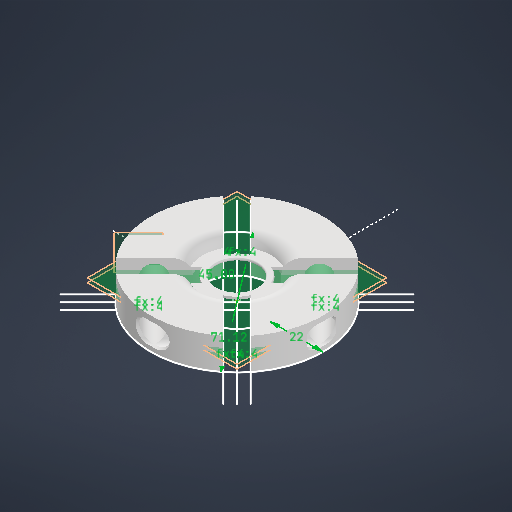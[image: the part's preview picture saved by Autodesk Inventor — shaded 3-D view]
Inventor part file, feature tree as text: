
AUTODESK INVENTOR PART (.ipt)
format: ipt  version: 2025 (Build 290162010, 162A)  size: 385,536 bytes
history: native  units: mm
features: extrude x4, sketch x3, plane x3, fillet x3, mirror x2
ambient origin geometry x8: Origin, YZ Plane, XZ Plane, XY Plane, X Axis, Y Axis, Z Axis, Center Point
bodies: Solid1 (feature_tree)
feature tree (15):
  sketch  "Sketch1"  dims[d0=71.12mm d1=22.0mm]
  extrude  "Extrusion1"  Depth=22.0mm
  extrude  "Extrusion2"  TaperAngle=45.0deg  [1 undecoded]
  plane  "Work Plane1"
  extrude  "Extrusion3"  Depth=0.5mm
  mirror  "Mirror1"
  mirror  "Mirror2"
  fillet  "Fillet1"  Radius=4.0mm
  plane  "Work Plane3"
  extrude  "Extrusion5"  Depth=0.5mm
  fillet  "Fillet3"  Radius=4.0mm
  fillet  "Fillet4"  Radius=4.0mm
  sketch  "Sketch2"  dims[d2=13.0mm d3=0.0mm d4=45.0deg]
  plane  "Work Plane2"
  sketch  "Sketch4"  dims[d5=4.0mm d6=4.0mm d7=4.0mm d8=4.0mm d9=4.0mm d10=4.0mm d11=4.0mm d12=4.0mm d13=13.0mm d14=0.0mm d15=20.0mm d16=9.0mm d17=13.0mm d18=50.0mm d19=0.0mm d20=0.0mm d21=6.0mm d22=-1.75mm d28=22.0mm d29=1.0mm d30=0.0mm d32=0.5mm d33=17.0mm d34=0.5mm]
note: 1 required parameter value undecoded (feature->parameter linkage not recoverable at this tier; creation-order binding heuristic only, values carry confidence <= 0.55)
